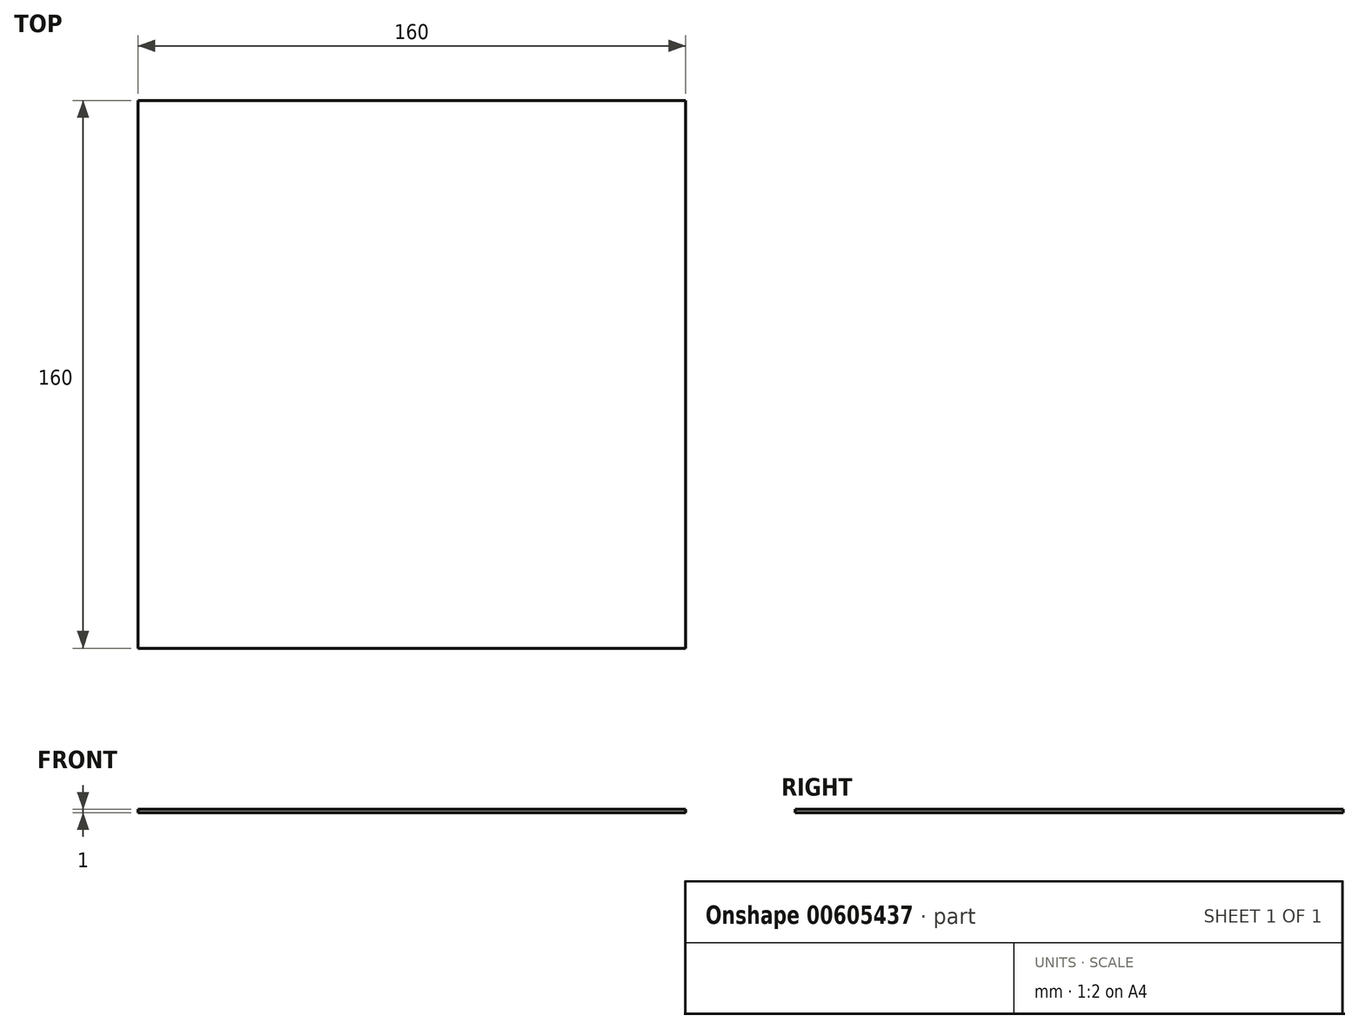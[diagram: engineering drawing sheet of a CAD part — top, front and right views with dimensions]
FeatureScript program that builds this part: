
annotation { "Feature Type Name" : "Feature", "Feature Type Description" : "" }
export const myFeature = defineFeature(function(context is Context, id is Id, definition is map)
    precondition{}
    {
        {
            var Q0;
            Q0=qCreatedBy(makeId("Top.planeOp"),FACE);
            var sketch = newSketch(context, id + "F0", { "sketchPlane" : qUnion([Q0])});
            skLineSegment(sketch, "E0.bottom", {"start": v(80, -80) * mm, "end": v(-80, -80) * mm});
            skLineSegment(sketch, "E0.top", {"start": v(80, 80) * mm, "end": v(-80, 80) * mm});
            skLineSegment(sketch, "E0.left", {"start": v(80, -80) * mm, "end": v(80, 80) * mm});
            skLineSegment(sketch, "E0.right", {"start": v(-80, -80) * mm, "end": v(-80, 80) * mm});
            skPoint(sketch, "E0.middle", {"position": v(0, 0) * mm});
            skSolve(sketch);
        }
        {
            var Q0;
            Q0=makeQuery(id+"F0.imprint","IMPRINT",FACE,{"disambiguationData":[TD([[makeQuery(id+"F0.imprint","IMPRINT",EDGE,{"derivedFrom":sQuery(id+"F0.wireOp",EDGE,"E0.bottom")}),-1.0]])]});
            extrude(context, id + "F1", {"entities" : qUnion([Q0]), "oppositeDirection" : true, "depth" : 1 * mm, "offsetDistance" : 25 * mm});
        }
    });
